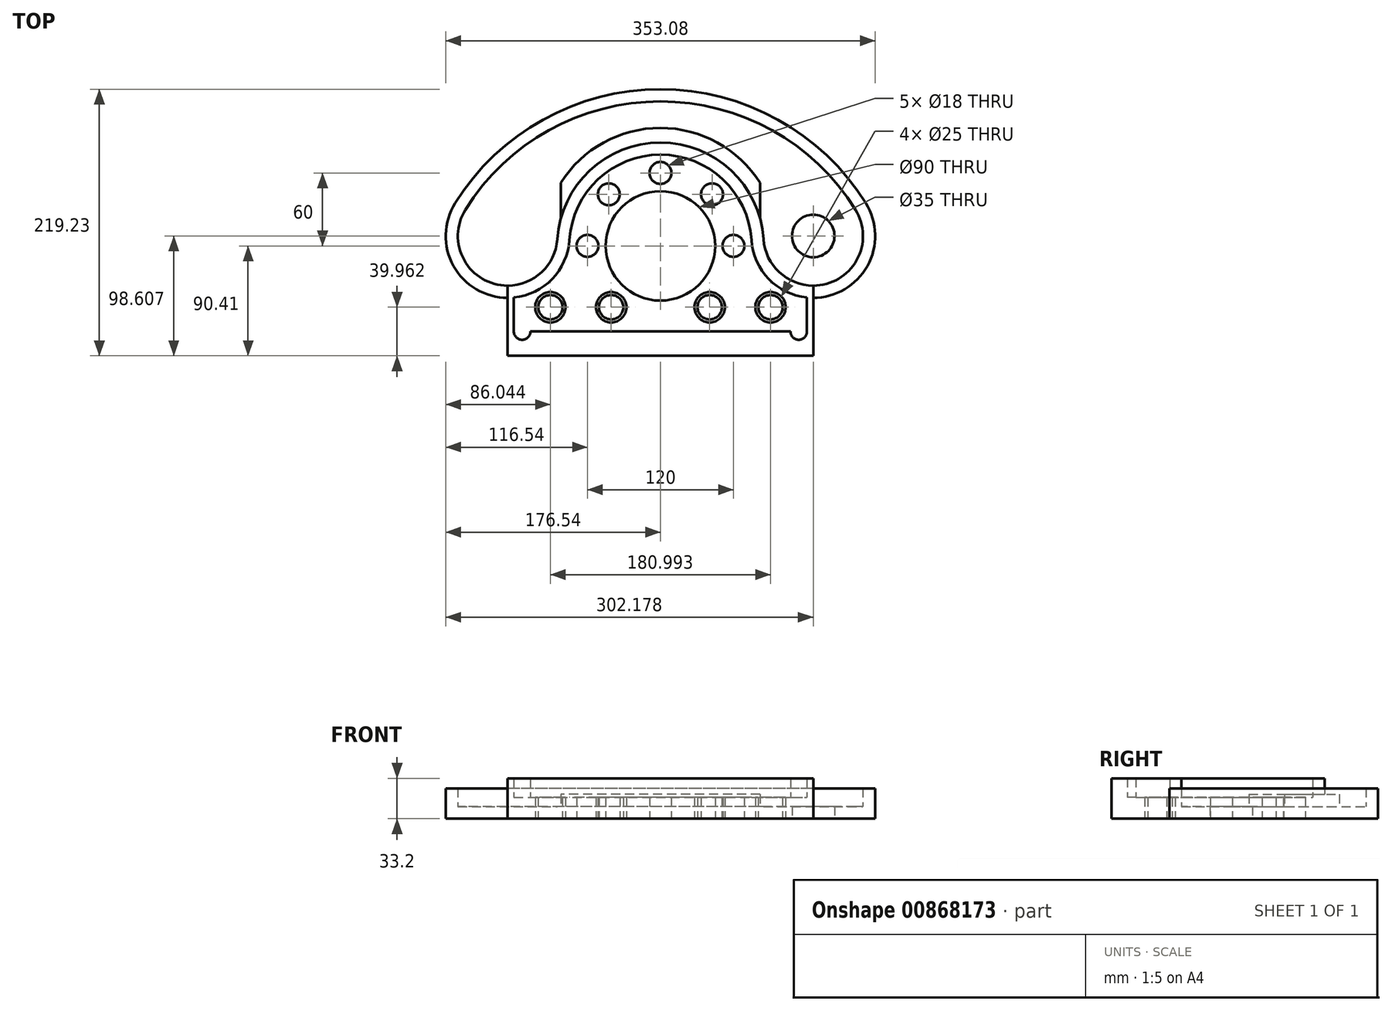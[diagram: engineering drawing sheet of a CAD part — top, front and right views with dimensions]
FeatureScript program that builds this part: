
annotation { "Feature Type Name" : "Feature", "Feature Type Description" : "" }
export const myFeature = defineFeature(function(context is Context, id is Id, definition is map)
    precondition{}
    {
        {
            var Q0;
            Q0=qCreatedBy(makeId("Top.planeOp"),FACE);
            var sketch = newSketch(context, id + "F0", { "sketchPlane" : qUnion([Q0])});
            skCircle(sketch, "E0", {"center": v(0, 0) * mm, "radius": 45 * mm});
            skArc(sketch, "E1", {"start": v(74.84, 4.88) * mm, "mid": v(0, 75) * mm, "end": v(-74.84, 4.88) * mm});
            skArc(sketch, "E2", {"start": v(84.82, 5.53) * mm, "mid": v(0, 85) * mm, "end": v(-84.82, 5.53) * mm});
            skLineSegment(sketch, "E3", {"start": v(-125.64, -32.7) * mm, "end": v(-125.64, -90.4) * mm});
            skLineSegment(sketch, "E4", {"start": v(-125.64, -90.4) * mm, "end": v(0, -90.4) * mm});
            skArc(sketch, "E5", {"start": v(-125.64, -32.7) * mm, "mid": v(-97.67, -21.65) * mm, "end": v(-84.82, 5.53) * mm});
            skArc(sketch, "E6", {"start": v(-120.5, -42.45) * mm, "mid": v(-89, -27.14) * mm, "end": v(-74.84, 4.88) * mm});
            skLineSegment(sketch, "E7", {"start": v(-120.5, -42.45) * mm, "end": v(-120.5, -70.4) * mm});
            skArc(sketch, "E8", {"start": v(-120.5, -70.4) * mm, "mid": v(-113.7, -77.21) * mm, "end": v(-106.9, -70.4) * mm});
            skLineSegment(sketch, "E9", {"start": v(-106.9, -70.4) * mm, "end": v(0, -70.4) * mm});
            skArc(sketch, "E10.MirrorCS", {"start": v(125.64, -32.7) * mm, "mid": v(97.67, -21.65) * mm, "end": v(84.82, 5.53) * mm});
            skArc(sketch, "E11.MirrorCS", {"start": v(120.5, -42.45) * mm, "mid": v(89, -27.14) * mm, "end": v(74.84, 4.88) * mm});
            skLineSegment(sketch, "E12.MirrorCS", {"start": v(125.64, -32.7) * mm, "end": v(125.64, -90.4) * mm});
            skLineSegment(sketch, "E13.MirrorCS", {"start": v(120.5, -42.45) * mm, "end": v(120.5, -70.4) * mm});
            skArc(sketch, "E14.MirrorCS", {"start": v(120.5, -70.4) * mm, "mid": v(113.7, -77.21) * mm, "end": v(106.9, -70.4) * mm});
            skLineSegment(sketch, "E15.MirrorCS", {"start": v(106.9, -70.4) * mm, "end": v(0, -70.4) * mm});
            skLineSegment(sketch, "E16.MirrorCS", {"start": v(125.64, -90.4) * mm, "end": v(0, -90.4) * mm});
            skPoint(sketch, "E17.orphan", {"position": v(125.64, -42.7) * mm});
            skPoint(sketch, "E18.orphan", {"position": v(-125.64, -42.7) * mm});
            skSolve(sketch);
        }
        {
            var Q0;
            {var subQ2=sQuery(id+"F0.wireOp",EDGE,"E1");Q0=makeQuery(id+"F0.imprint","IMPRINT",FACE,{"disambiguationData":[TD([[makeQuery(id+"F0.imprint","IMPRINT",EDGE,{"derivedFrom":subQ2}),-1.0]])]});}
            var Q1;
            Q1=makeQuery(id+"F0.imprint","IMPRINT",FACE,{"disambiguationData":[TD([[makeQuery(id+"F0.imprint","IMPRINT",EDGE,{"derivedFrom":sQuery(id+"F0.wireOp",EDGE,"E0")}),-1.0]])]});
            extrude(context, id + "F1", {"entities" : qUnion([Q0, Q1]), "depth" : 17.5 * mm, "offsetDistance" : 25 * mm});
        }
        {
            var Q0;
            {var subQ2=sQuery(id+"F0.wireOp",EDGE,"E1");Q0=makeQuery(id+"F0.imprint","IMPRINT",FACE,{"disambiguationData":[TD([[makeQuery(id+"F0.imprint","IMPRINT",EDGE,{"derivedFrom":subQ2}),-1.0]])]});}
            extrude(context, id + "F2", {"entities" : qUnion([Q0]), "operationType" : NewBodyOperationType.ADD, "depth" : 33.2 * mm, "offsetDistance" : 25 * mm});
        }
        {
            var Q0;
            Q0=qCreatedBy(makeId("Top.planeOp"),FACE);
            var sketch = newSketch(context, id + "F3", { "sketchPlane" : qUnion([Q0])});
            skArc(sketch, "E19", {"start": v(81.93, 51.92) * mm, "mid": v(0, 97) * mm, "end": v(-81.93, 51.92) * mm});
            skLineSegment(sketch, "E20", {"start": v(-81.93, 22.63) * mm, "end": v(-81.93, 51.92) * mm});
            skArc(sketch, "E21.0", {"start": v(84.82, 5.53) * mm, "mid": v(0, 85) * mm, "end": v(-84.82, 5.53) * mm});
            skLineSegment(sketch, "E22.MirrorCS", {"start": v(81.93, 22.63) * mm, "end": v(81.93, 51.92) * mm});
            skPoint(sketch, "E23.orphan", {"position": v(-81.93, 0) * mm});
            skPoint(sketch, "E24.orphan", {"position": v(81.93, 0) * mm});
            skSolve(sketch);
        }
        {
            var Q0;
            Q0=makeQuery(id+"F3.imprint","IMPRINT",FACE,{"disambiguationData":[TD([[makeQuery(id+"F3.imprint","IMPRINT",EDGE,{"derivedFrom":sQuery(id+"F3.wireOp",EDGE,"E19")}),1.0]])]});
            extrude(context, id + "F4", {"entities" : qUnion([Q0]), "operationType" : NewBodyOperationType.ADD, "depth" : 20 * mm, "offsetDistance" : 25 * mm});
        }
        {
            var Q0;
            Q0=qCreatedBy(makeId("Top.planeOp"),FACE);
            var sketch = newSketch(context, id + "F5", { "sketchPlane" : qUnion([Q0])});
            skPoint(sketch, "E25.0", {"position": v(125.64, 8.2) * mm});
            skPoint(sketch, "E26.0", {"position": v(125.64, -32.7) * mm});
            skArc(sketch, "E27", {"start": v(125.64, -32.7) * mm, "mid": v(161.4, -11.65) * mm, "end": v(160.35, 29.84) * mm});
            skArc(sketch, "E28", {"start": v(160.35, 29.84) * mm, "mid": v(91.69, 95.08) * mm, "end": v(0, 118.82) * mm});
            skArc(sketch, "E29.MirrorCS", {"start": v(-160.35, 29.84) * mm, "mid": v(-91.69, 95.08) * mm, "end": v(0, 118.82) * mm});
            skArc(sketch, "E30.MirrorC", {"start": v(-125.64, -32.7) * mm, "mid": v(-161.4, -11.65) * mm, "end": v(-160.35, 29.84) * mm});
            skArc(sketch, "E31.0", {"start": v(-125.64, -32.7) * mm, "mid": v(-97.67, -21.65) * mm, "end": v(-84.82, 5.53) * mm});
            skPoint(sketch, "E32.0", {"position": v(-81.93, 37.27) * mm});
            skArc(sketch, "E33.0", {"start": v(81.93, 51.92) * mm, "mid": v(0, 97) * mm, "end": v(-81.93, 51.92) * mm});
            skPoint(sketch, "E34.0", {"position": v(81.93, 37.27) * mm});
            skPoint(sketch, "E35.0", {"position": v(97.67, -21.65) * mm});
            skPoint(sketch, "E36.0", {"position": v(84.82, 5.53) * mm});
            skArc(sketch, "E37.0", {"start": v(125.64, -32.7) * mm, "mid": v(97.67, -21.65) * mm, "end": v(84.82, 5.53) * mm});
            skPoint(sketch, "E38.0", {"position": v(81.93, 22.63) * mm});
            skPoint(sketch, "E39.0", {"position": v(83.81, 14.15) * mm});
            skArc(sketch, "E40.0", {"start": v(84.82, 5.53) * mm, "mid": v(83.81, 14.15) * mm, "end": v(81.93, 22.63) * mm});
            skLineSegment(sketch, "E41.0", {"start": v(81.93, 22.63) * mm, "end": v(81.93, 51.92) * mm});
            skLineSegment(sketch, "E42.0", {"start": v(-81.93, 22.63) * mm, "end": v(-81.93, 51.92) * mm});
            skPoint(sketch, "E43.0", {"position": v(-81.93, 22.63) * mm});
            skPoint(sketch, "E44.0.end.orphan", {"position": v(-84.82, 5.53) * mm});
            skArc(sketch, "E45.0", {"start": v(-81.93, 22.63) * mm, "mid": v(-83.81, 14.15) * mm, "end": v(-84.82, 5.53) * mm});
            skSolve(sketch);
        }
        {
            var Q0;
            Q0=qSketchRegion(id+"F5",true);
            extrude(context, id + "F6", {"entities" : qUnion([Q0]), "operationType" : NewBodyOperationType.ADD, "depth" : 10 * mm, "offsetDistance" : 25 * mm});
        }
        {
            var Q0;
            Q0=makeQuery(id+"F0.imprint","IMPRINT",FACE,{"disambiguationData":[TD([[makeQuery(id+"F0.imprint","IMPRINT",EDGE,{"derivedFrom":sQuery(id+"F0.wireOp",EDGE,"E0")}),1.0]])]});
            var sketch = newSketch(context, id + "F7", { "sketchPlane" : qUnion([Q0])});
            skPoint(sketch, "E46.0", {"position": v(125.64, -90.4) * mm});
            skPoint(sketch, "E47.0", {"position": v(120.5, -42.45) * mm});
            skPoint(sketch, "E48.0", {"position": v(125.64, 8.2) * mm});
            skPoint(sketch, "E49.0", {"position": v(-120.5, -42.45) * mm});
            skPoint(sketch, "E50.0", {"position": v(-125.64, 8.2) * mm});
            skPoint(sketch, "E51.0", {"position": v(-125.64, -90.4) * mm});
            skPoint(sketch, "E52.0", {"position": v(0, -70.15) * mm});
            skArc(sketch, "E53", {"start": v(125.64, -42.7) * mm, "mid": v(170.15, -16.5) * mm, "end": v(168.83, 35.13) * mm});
            skArc(sketch, "E54", {"start": v(-168.83, 35.13) * mm, "mid": v(-170.15, -16.5) * mm, "end": v(-125.64, -42.7) * mm});
            skArc(sketch, "E55", {"start": v(168.83, 35.13) * mm, "mid": v(0, 128.82) * mm, "end": v(-168.83, 35.13) * mm});
            skPoint(sketch, "E56.0", {"position": v(-125.64, -32.7) * mm});
            skPoint(sketch, "E57.0", {"position": v(-125.64, -42.7) * mm});
            skPoint(sketch, "E58.0", {"position": v(125.64, -32.7) * mm});
            skPoint(sketch, "E59.0", {"position": v(125.64, -42.7) * mm});
            skLineSegment(sketch, "E60", {"start": v(125.64, -42.7) * mm, "end": v(125.64, -32.7) * mm});
            skLineSegment(sketch, "E61", {"start": v(-125.64, -42.7) * mm, "end": v(-125.64, -32.7) * mm});
            skArc(sketch, "E62.2", {"start": v(125.64, -32.7) * mm, "mid": v(161.4, -11.65) * mm, "end": v(160.35, 29.84) * mm});
            skArc(sketch, "E62.3", {"start": v(160.35, 29.84) * mm, "mid": v(91.69, 95.08) * mm, "end": v(0, 118.82) * mm});
            skArc(sketch, "E62.4", {"start": v(-160.35, 29.84) * mm, "mid": v(-91.69, 95.08) * mm, "end": v(0, 118.82) * mm});
            skArc(sketch, "E62.5", {"start": v(-125.64, -32.7) * mm, "mid": v(-161.4, -11.65) * mm, "end": v(-160.35, 29.84) * mm});
            skPoint(sketch, "E62.9", {"position": v(-161.4, -11.65) * mm});
            skSolve(sketch);
        }
        {
            var Q0;
            Q0=makeQuery(id+"F7.imprint","IMPRINT",FACE,{"disambiguationData":[TD([[makeQuery(id+"F7.imprint","IMPRINT",EDGE,{"derivedFrom":sQuery(id+"F7.wireOp",EDGE,"E53")}),1.0]])]});
            extrude(context, id + "F8", {"entities" : qUnion([Q0]), "operationType" : NewBodyOperationType.ADD, "depth" : 25 * mm, "offsetDistance" : 25 * mm});
        }
        {
            var Q0;
            Q0=makeQuery(id+"F0.imprint","IMPRINT",FACE,{"disambiguationData":[TD([[makeQuery(id+"F0.imprint","IMPRINT",EDGE,{"derivedFrom":sQuery(id+"F0.wireOp",EDGE,"E0")}),1.0]])]});
            var sketch = newSketch(context, id + "F9", { "sketchPlane" : qUnion([Q0])});
            skPoint(sketch, "E63.0", {"position": v(125.64, 8.2) * mm});
            skPoint(sketch, "E64.0", {"position": v(-125.64, 8.2) * mm});
            skCircle(sketch, "E65", {"center": v(125.64, 8.2) * mm, "radius": 17.5 * mm});
            skPoint(sketch, "E66.0", {"position": v(120.5, -56.43) * mm});
            skPoint(sketch, "E67.0", {"position": v(-120.5, -56.43) * mm});
            skPoint(sketch, "E68.0", {"position": v(-120.5, -42.45) * mm});
            skPoint(sketch, "E69.0", {"position": v(120.5, -42.45) * mm});
            skLineSegment(sketch, "E70", {"start": v(-120.5, -42.45) * mm, "end": v(-120.5, -50.45) * mm});
            skLineSegment(sketch, "E71", {"start": v(-120.5, -50.45) * mm, "end": v(120.5, -50.45) * mm});
            skLineSegment(sketch, "E72", {"start": v(-120.5, -50.45) * mm, "end": v(-90.5, -50.45) * mm});
            skLineSegment(sketch, "E73", {"start": v(-90.5, -50.45) * mm, "end": v(9.5, -50.45) * mm});
            skLineSegment(sketch, "E74", {"start": v(-90.5, -50.45) * mm, "end": v(-40.5, -50.45) * mm});
            skLineSegment(sketch, "E75", {"start": v(120.5, -50.45) * mm, "end": v(90.5, -50.45) * mm});
            skLineSegment(sketch, "E76", {"start": v(90.5, -50.45) * mm, "end": v(40.5, -50.45) * mm});
            skCircle(sketch, "E77", {"center": v(-90.5, -50.45) * mm, "radius": 12.5 * mm});
            skCircle(sketch, "E78", {"center": v(-40.5, -50.45) * mm, "radius": 12.5 * mm});
            skCircle(sketch, "E79", {"center": v(40.5, -50.45) * mm, "radius": 12.5 * mm});
            skCircle(sketch, "E80", {"center": v(90.5, -50.45) * mm, "radius": 12.5 * mm});
            skCircle(sketch, "E81", {"center": v(-90.5, -50.45) * mm, "radius": 10 * mm});
            skCircle(sketch, "E82", {"center": v(-40.5, -50.45) * mm, "radius": 10 * mm});
            skCircle(sketch, "E83", {"center": v(40.5, -50.45) * mm, "radius": 10 * mm});
            skCircle(sketch, "E84", {"center": v(90.5, -50.45) * mm, "radius": 10 * mm});
            skSolve(sketch);
        }
        {
            var Q0;
            Q0=makeQuery(id+"F9.imprint","IMPRINT",FACE,{"disambiguationData":[TD([[makeQuery(id+"F9.imprint","IMPRINT",EDGE,{"derivedFrom":sQuery(id+"F9.wireOp",EDGE,"E65")}),1.0]])]});
            extrude(context, id + "F10", {"entities" : qUnion([Q0]), "operationType" : NewBodyOperationType.REMOVE, "depth" : 25 * mm, "offsetDistance" : 25 * mm});
        }
        {
            var Q0;
            Q0=makeQuery(id+"F0.imprint","IMPRINT",FACE,{"disambiguationData":[TD([[makeQuery(id+"F0.imprint","IMPRINT",EDGE,{"derivedFrom":sQuery(id+"F0.wireOp",EDGE,"E0")}),1.0]])]});
            var sketch = newSketch(context, id + "F11", { "sketchPlane" : qUnion([Q0])});
            skCircle(sketch, "E85.0", {"center": v(0, 0) * mm, "radius": 45 * mm});
            skLineSegment(sketch, "E86.0.0", {"start": v(-106.9, -70.4) * mm, "end": v(106.9, -70.4) * mm});
            skArc(sketch, "E86.0.1", {"start": v(106.9, -70.4) * mm, "mid": v(113.7, -77.21) * mm, "end": v(120.5, -70.4) * mm});
            skLineSegment(sketch, "E86.0.2", {"start": v(120.5, -70.4) * mm, "end": v(120.5, -42.45) * mm});
            skArc(sketch, "E86.0.3", {"start": v(120.5, -42.45) * mm, "mid": v(89, -27.14) * mm, "end": v(74.84, 4.88) * mm});
            skArc(sketch, "E86.0.4", {"start": v(-74.84, 4.88) * mm, "mid": v(0, 75) * mm, "end": v(74.84, 4.88) * mm});
            skArc(sketch, "E86.0.5", {"start": v(-74.84, 4.88) * mm, "mid": v(-89, -27.14) * mm, "end": v(-120.5, -42.45) * mm});
            skLineSegment(sketch, "E86.0.6", {"start": v(-120.5, -42.45) * mm, "end": v(-120.5, -70.4) * mm});
            skArc(sketch, "E86.0.7", {"start": v(-106.9, -70.4) * mm, "mid": v(-113.7, -77.21) * mm, "end": v(-120.5, -70.4) * mm});
            skLineSegment(sketch, "E87", {"start": v(0, 0) * mm, "end": v(0, 45) * mm});
            skLineSegment(sketch, "E88", {"start": v(0, 45) * mm, "end": v(0, 60) * mm});
            skLineSegment(sketch, "E89", {"start": v(0, 0) * mm, "end": v(45, 0) * mm});
            skLineSegment(sketch, "E90", {"start": v(0, 0) * mm, "end": v(-45, 0) * mm});
            skLineSegment(sketch, "E91", {"start": v(-45, 0) * mm, "end": v(-60, 0) * mm});
            skLineSegment(sketch, "E92", {"start": v(45, 0) * mm, "end": v(60, 0) * mm});
            skCircle(sketch, "E93", {"center": v(0, 60) * mm, "radius": 9 * mm});
            skCircle(sketch, "E94", {"center": v(60, 0) * mm, "radius": 9 * mm});
            skCircle(sketch, "E95", {"center": v(-60, 0) * mm, "radius": 9 * mm});
            skCircle(sketch, "E96", {"center": v(42.43, 42.43) * mm, "radius": 9 * mm});
            skCircle(sketch, "E97", {"center": v(-42.43, 42.43) * mm, "radius": 9 * mm});
            skSolve(sketch);
        }
        {
            var Q0;
            Q0=makeQuery(id+"F11.imprint","IMPRINT",FACE,{"disambiguationData":[TD([[makeQuery(id+"F11.imprint","IMPRINT",EDGE,{"derivedFrom":sQuery(id+"F11.wireOp",EDGE,"E95")}),1.0]])]});
            var Q1;
            Q1=makeQuery(id+"F11.imprint","IMPRINT",FACE,{"disambiguationData":[TD([[makeQuery(id+"F11.imprint","IMPRINT",EDGE,{"derivedFrom":sQuery(id+"F11.wireOp",EDGE,"E97")}),1.0]])]});
            var Q2;
            Q2=makeQuery(id+"F11.imprint","IMPRINT",FACE,{"disambiguationData":[TD([[makeQuery(id+"F11.imprint","IMPRINT",EDGE,{"derivedFrom":sQuery(id+"F11.wireOp",EDGE,"E93")}),1.0]])]});
            var Q3;
            Q3=makeQuery(id+"F11.imprint","IMPRINT",FACE,{"disambiguationData":[TD([[makeQuery(id+"F11.imprint","IMPRINT",EDGE,{"derivedFrom":sQuery(id+"F11.wireOp",EDGE,"E96")}),1.0]])]});
            var Q4;
            Q4=makeQuery(id+"F11.imprint","IMPRINT",FACE,{"disambiguationData":[TD([[makeQuery(id+"F11.imprint","IMPRINT",EDGE,{"derivedFrom":sQuery(id+"F11.wireOp",EDGE,"E94")}),1.0]])]});
            var Q5;
            Q5=sQuery(id+"F11.wireOp",EDGE,"E97");
            var Q6;
            Q6=sQuery(id+"F11.wireOp",EDGE,"E93");
            var Q7;
            Q7=sQuery(id+"F11.wireOp",EDGE,"E96");
            var Q8;
            Q8=sQuery(id+"F11.wireOp",EDGE,"E94");
            var Q9;
            Q9=sQuery(id+"F11.wireOp",EDGE,"E95");
            extrude(context, id + "F12", {"entities" : qUnion([Q0, Q1, Q2, Q3, Q4]), "operationType" : NewBodyOperationType.REMOVE, "surfaceEntities" : qUnion([Q5, Q6, Q7, Q8, Q9]), "depth" : 25 * mm, "offsetDistance" : 25 * mm});
        }
        {
            var Q0;
            {var subQ0=sQuery(id+"F9.wireOp",EDGE,"E76");var subQ1=sQuery(id+"F9.wireOp",EDGE,"E75");var subQ2=makeQuery(id+"F9.imprint","INTERSECT",VERTEX,{"derivedFrom":[subQ1,subQ0]});Q0=makeQuery(id+"F9.imprint","IMPRINT",FACE,{"disambiguationData":[TD([[makeQuery(id+"F9.imprint","IMPRINT",EDGE,{"disambiguationData":[TD([[subQ2,1.0]])],"derivedFrom":subQ1}),1.0]])]});}
            var Q1;
            {var subQ0=sQuery(id+"F9.wireOp",EDGE,"E76");var subQ1=sQuery(id+"F9.wireOp",EDGE,"E75");var subQ2=makeQuery(id+"F9.imprint","INTERSECT",VERTEX,{"derivedFrom":[subQ1,subQ0]});Q1=makeQuery(id+"F9.imprint","IMPRINT",FACE,{"disambiguationData":[TD([[makeQuery(id+"F9.imprint","IMPRINT",EDGE,{"disambiguationData":[TD([[subQ2,1.0]])],"derivedFrom":subQ1}),-1.0]])]});}
            var Q2;
            {var subQ0=sQuery(id+"F9.wireOp",EDGE,"E76");var subQ1=sQuery(id+"F9.wireOp",EDGE,"E71");var subQ2=makeQuery(id+"F9.imprint","INTERSECT",VERTEX,{"derivedFrom":[subQ1,subQ0]});Q2=makeQuery(id+"F9.imprint","IMPRINT",FACE,{"disambiguationData":[TD([[makeQuery(id+"F9.imprint","IMPRINT",EDGE,{"disambiguationData":[TD([[subQ2,1.0]])],"derivedFrom":subQ1}),1.0]])]});}
            var Q3;
            {var subQ0=sQuery(id+"F9.wireOp",EDGE,"E76");var subQ1=sQuery(id+"F9.wireOp",EDGE,"E71");var subQ2=makeQuery(id+"F9.imprint","INTERSECT",VERTEX,{"derivedFrom":[subQ1,subQ0]});Q3=makeQuery(id+"F9.imprint","IMPRINT",FACE,{"disambiguationData":[TD([[makeQuery(id+"F9.imprint","IMPRINT",EDGE,{"disambiguationData":[TD([[subQ2,1.0]])],"derivedFrom":subQ1}),-1.0]])]});}
            var Q4;
            {var subQ0=sQuery(id+"F9.wireOp",EDGE,"E74");var subQ1=sQuery(id+"F9.wireOp",EDGE,"E73");var subQ2=makeQuery(id+"F9.imprint","INTERSECT",VERTEX,{"derivedFrom":[subQ1,subQ0]});Q4=makeQuery(id+"F9.imprint","IMPRINT",FACE,{"disambiguationData":[TD([[makeQuery(id+"F9.imprint","IMPRINT",EDGE,{"disambiguationData":[TD([[subQ2,-1.0]])],"derivedFrom":subQ1}),1.0]])]});}
            var Q5;
            {var subQ0=sQuery(id+"F9.wireOp",EDGE,"E74");var subQ1=sQuery(id+"F9.wireOp",EDGE,"E73");var subQ2=makeQuery(id+"F9.imprint","INTERSECT",VERTEX,{"derivedFrom":[subQ1,subQ0]});Q5=makeQuery(id+"F9.imprint","IMPRINT",FACE,{"disambiguationData":[TD([[makeQuery(id+"F9.imprint","IMPRINT",EDGE,{"disambiguationData":[TD([[subQ2,-1.0]])],"derivedFrom":subQ1}),-1.0]])]});}
            var Q6;
            {var subQ0=sQuery(id+"F9.wireOp",EDGE,"E74");var subQ1=sQuery(id+"F9.wireOp",EDGE,"E72");var subQ2=makeQuery(id+"F9.imprint","INTERSECT",VERTEX,{"derivedFrom":[subQ1,subQ0]});Q6=makeQuery(id+"F9.imprint","IMPRINT",FACE,{"disambiguationData":[TD([[makeQuery(id+"F9.imprint","IMPRINT",EDGE,{"disambiguationData":[TD([[subQ2,1.0]])],"derivedFrom":subQ1}),1.0]])]});}
            var Q7;
            {var subQ0=sQuery(id+"F9.wireOp",EDGE,"E74");var subQ1=sQuery(id+"F9.wireOp",EDGE,"E72");var subQ2=makeQuery(id+"F9.imprint","INTERSECT",VERTEX,{"derivedFrom":[subQ1,subQ0]});Q7=makeQuery(id+"F9.imprint","IMPRINT",FACE,{"disambiguationData":[TD([[makeQuery(id+"F9.imprint","IMPRINT",EDGE,{"disambiguationData":[TD([[subQ2,1.0]])],"derivedFrom":subQ1}),-1.0]])]});}
            var Q8;
            Q8=sQuery(id+"F9.wireOp",EDGE,"E84");
            var Q9;
            Q9=sQuery(id+"F9.wireOp",EDGE,"E83");
            var Q10;
            Q10=sQuery(id+"F9.wireOp",EDGE,"E82");
            var Q11;
            Q11=sQuery(id+"F9.wireOp",EDGE,"E81");
            extrude(context, id + "F13", {"entities" : qUnion([Q0, Q1, Q2, Q3, Q4, Q5, Q6, Q7]), "operationType" : NewBodyOperationType.REMOVE, "surfaceEntities" : qUnion([Q8, Q9, Q10, Q11]), "depth" : 25 * mm, "offsetDistance" : 25 * mm});
        }
    });
